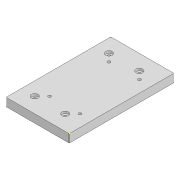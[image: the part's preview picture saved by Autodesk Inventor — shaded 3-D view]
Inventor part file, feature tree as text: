
AUTODESK INVENTOR PART (.ipt)
format: ipt  version: 2020 (Build 240168000, 168)  size: 225,792 bytes
history: native  units: mm
features: sketch x8, extrude x7, other x4, fillet x1
ambient origin geometry x8: Origin, YZ Plane, XZ Plane, XY Plane, X Axis, Y Axis, Z Axis, Center Point
bodies: Body1 (feature_tree)
feature tree (20):
  other  "Sólido1"
  extrude  "Extrusão1"  Depth=140.0mm
  extrude  "Extrusão2"  Depth=4.0mm
  sketch  "Esboço3"  dims[d4=4.0mm d5=4.0mm]
  extrude  "Extrusão3"  Depth=4.0mm
  extrude  "Extrusão4"  Depth=10.0mm
  extrude  "Extrusão5"  Depth=20.0mm
  extrude  "Extrusão6"  Depth=20.0mm
  extrude  "Extrusão7"  Depth=11.0mm
  fillet  "Arredondamento1"  Radius=11.0mm
  sketch  "Esboço1"  dims[d0=77.0mm d1=140.0mm]
  sketch  "Esboço2"  dims[d2=4.0mm d3=4.0mm]
  sketch  "Esboço4"  dims[d6=10.0mm d7=10.0mm]
  sketch  "Esboço5"  dims[d8=20.0mm d9=20.0mm]
  sketch  "Esboço6"  dims[d10=20.0mm d11=20.0mm]
  other  "Contorno projetado1"
  sketch  "Esboço7"  dims[d12=26.0mm d13=26.0mm d14=11.0mm d15=0.0mm]
  other  "Contorno projetado2"
  sketch  "Esboço8"  dims[d16=9.0mm d17=9.0mm d18=9.0mm d19=9.0mm d20=3.0mm d21=0.0mm d22=4.0mm d23=4.0mm d24=10.0mm d25=10.0mm d26=10.0mm d27=10.0mm d28=4.0mm d29=4.0mm d30=10.0mm d31=10.0mm d32=10.0mm d33=10.0mm d34=12.0mm d35=0.0mm d36=6.95mm d37=6.95mm d38=6.95mm d39=6.95mm d40=6.0mm d41=0.0mm d42=0.5mm d43=0.0mm d44=0.5mm d45=0.0mm d46=8.0mm d47=0.0mm d48=1.0mm]
  other  "Contorno projetado3"
